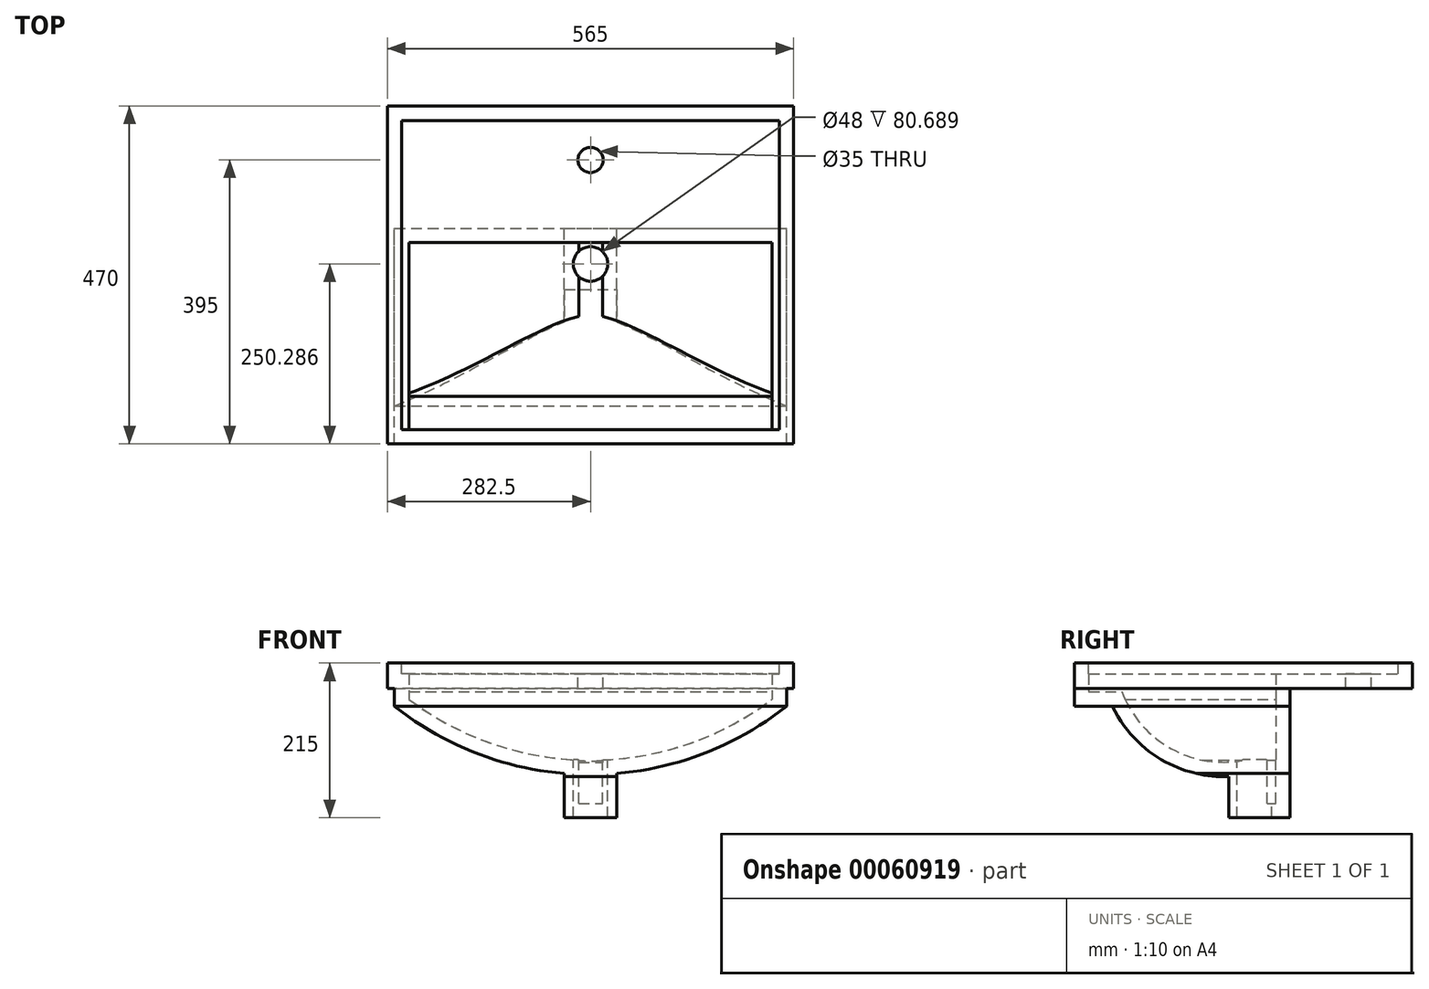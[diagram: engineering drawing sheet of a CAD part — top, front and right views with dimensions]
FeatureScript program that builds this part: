
annotation { "Feature Type Name" : "Feature", "Feature Type Description" : "" }
export const myFeature = defineFeature(function(context is Context, id is Id, definition is map)
    precondition{}
    {
        {
            var Q0;
            Q0=qCreatedBy(makeId("Front.planeOp"),FACE);
            var sketch = newSketch(context, id + "F0", { "sketchPlane" : qUnion([Q0])});
            skLineSegment(sketch, "E0.bottom", {"start": v(36.5, -107.5) * mm, "end": v(-36.5, -107.5) * mm});
            skLineSegment(sketch, "E0.top", {"start": v(282.5, 107.5) * mm, "end": v(-282.5, 107.5) * mm});
            skLineSegment(sketch, "E0.left", {"start": v(282.5, 72.5) * mm, "end": v(282.5, 107.5) * mm});
            skLineSegment(sketch, "E0.right", {"start": v(-282.5, 72.5) * mm, "end": v(-282.5, 107.5) * mm});
            skPoint(sketch, "E0.middle", {"position": v(0, 0) * mm});
            skLineSegment(sketch, "E1.bottom", {"start": v(-36.5, -107.5) * mm, "end": v(36.5, -107.5) * mm});
            skLineSegment(sketch, "E1.top", {"start": v(-36.5, -47.5) * mm, "end": v(36.5, -47.5) * mm});
            skLineSegment(sketch, "E1.left", {"start": v(-36.5, -107.5) * mm, "end": v(-36.5, -47.5) * mm});
            skLineSegment(sketch, "E1.right", {"start": v(36.5, -107.5) * mm, "end": v(36.5, -47.5) * mm});
            skLineSegment(sketch, "E2.bottom", {"start": v(-272.5, 72.5) * mm, "end": v(272.5, 72.5) * mm});
            skLineSegment(sketch, "E2.top", {"start": v(-272.5, 47.5) * mm, "end": v(272.5, 47.5) * mm});
            skLineSegment(sketch, "E2.left", {"start": v(-272.5, 72.5) * mm, "end": v(-272.5, 47.5) * mm});
            skLineSegment(sketch, "E2.right", {"start": v(272.5, 72.5) * mm, "end": v(272.5, 47.5) * mm});
            skLineSegment(sketch, "E3", {"start": v(-272.5, 72.5) * mm, "end": v(-282.5, 72.5) * mm});
            skLineSegment(sketch, "E4", {"start": v(272.5, 72.5) * mm, "end": v(282.5, 72.5) * mm});
            skArc(sketch, "E5", {"start": v(-272.5, 47.5) * mm, "mid": v(-144.3, -23.07) * mm, "end": v(0, -47.5) * mm});
            skArc(sketch, "E6", {"start": v(0, -47.5) * mm, "mid": v(144.3, -23.07) * mm, "end": v(272.5, 47.5) * mm});
            skLineSegment(sketch, "E7", {"start": v(-36.5, -47.5) * mm, "end": v(-36.5, -45.98) * mm});
            skLineSegment(sketch, "E8", {"start": v(36.5, -47.5) * mm, "end": v(36.5, -45.98) * mm});
            skSolve(sketch);
        }
        {
            var Q0;
            Q0 = qSketchRegion(id + "F0", true);
            extrude(context, id + "F1", {"entities" : qUnion([Q0]), "depth" : 470 * mm});
        }
        {
            var Q0;
            Q0=makeQuery(id+"F1.opExtrude","SWEPT_FACE",FACE,{"disambiguationData":[OSD([sQuery(id+"F0.wireOp",EDGE,"E2.right")])]});
            var sketch = newSketch(context, id + "F2", { "sketchPlane" : qUnion([Q0])});
            skLineSegment(sketch, "E9.bottom", {"start": v(0, 72.5) * mm, "end": v(-170, 72.5) * mm});
            skLineSegment(sketch, "E9.top", {"start": v(0, -107.5) * mm, "end": v(-170, -107.5) * mm});
            skLineSegment(sketch, "E9.left", {"start": v(0, 72.5) * mm, "end": v(0, -107.5) * mm});
            skLineSegment(sketch, "E9.right", {"start": v(-170, 72.5) * mm, "end": v(-170, -107.5) * mm});
            skLineSegment(sketch, "E10.bottom", {"start": v(-470, 47.5) * mm, "end": v(-417.05, 47.5) * mm});
            skLineSegment(sketch, "E10.top", {"start": v(-470, -107.5) * mm, "end": v(-417.05, -107.5) * mm});
            skLineSegment(sketch, "E10.left", {"start": v(-470, 47.5) * mm, "end": v(-470, -107.5) * mm});
            skLineSegment(sketch, "E10.right", {"start": v(-417.05, 47.5) * mm, "end": v(-417.05, -107.5) * mm});
            skArc(sketch, "E11", {"start": v(-417.05, 47.5) * mm, "mid": v(-350.73, -25.73) * mm, "end": v(-255.01, -50.16) * mm});
            skLineSegment(sketch, "E12", {"start": v(-255.01, -50.16) * mm, "end": v(-255.01, -107.5) * mm});
            skLineSegment(sketch, "E13", {"start": v(-417.05, -107.5) * mm, "end": v(-255.01, -107.5) * mm});
            skSolve(sketch);
        }
        {
            var Q0;
            Q0 = qSketchRegion(id + "F2", true);
            extrude(context, id + "F3", {"entities" : qUnion([Q0]), "operationType" : NewBodyOperationType.REMOVE, "endBound" : BoundingType.THROUGH_ALL, "oppositeDirection" : true, "depth" : 25 * mm});
        }
        {
            var Q0;
            Q0=makeQuery(id+"F1.opExtrude","SWEPT_FACE",FACE,{"disambiguationData":[OSD([sQuery(id+"F0.wireOp",EDGE,"E0.top")])]});
            shell(context, id + "F4", {"entities" : qUnion([Q0]), "thickness" : 20 * mm});
        }
        {
            var Q0;
            Q0=makeQuery(id+"F4.opShell","OFFSET_FACE",FACE,{"disambiguationData":[OSD([sQuery(id+"F0.wireOp",EDGE,"E3"),sQuery(id+"F0.wireOp",EDGE,"E4"),sQuery(id+"F2.wireOp",EDGE,"E9.bottom")])]});
            var sketch = newSketch(context, id + "F5", { "sketchPlane" : qUnion([Q0])});
            skCircle(sketch, "E14", {"center": v(0, -75) * mm, "radius": 17.5 * mm});
            skCircle(sketch, "E15", {"center": v(0, -219.71) * mm, "radius": 24 * mm});
            skSolve(sketch);
        }
        {
            var Q0;
            Q0 = qSketchRegion(id + "F5", true);
            extrude(context, id + "F6", {"entities" : qUnion([Q0]), "operationType" : NewBodyOperationType.REMOVE, "endBound" : BoundingType.THROUGH_ALL, "oppositeDirection" : true, "depth" : 25 * mm});
        }
    });
